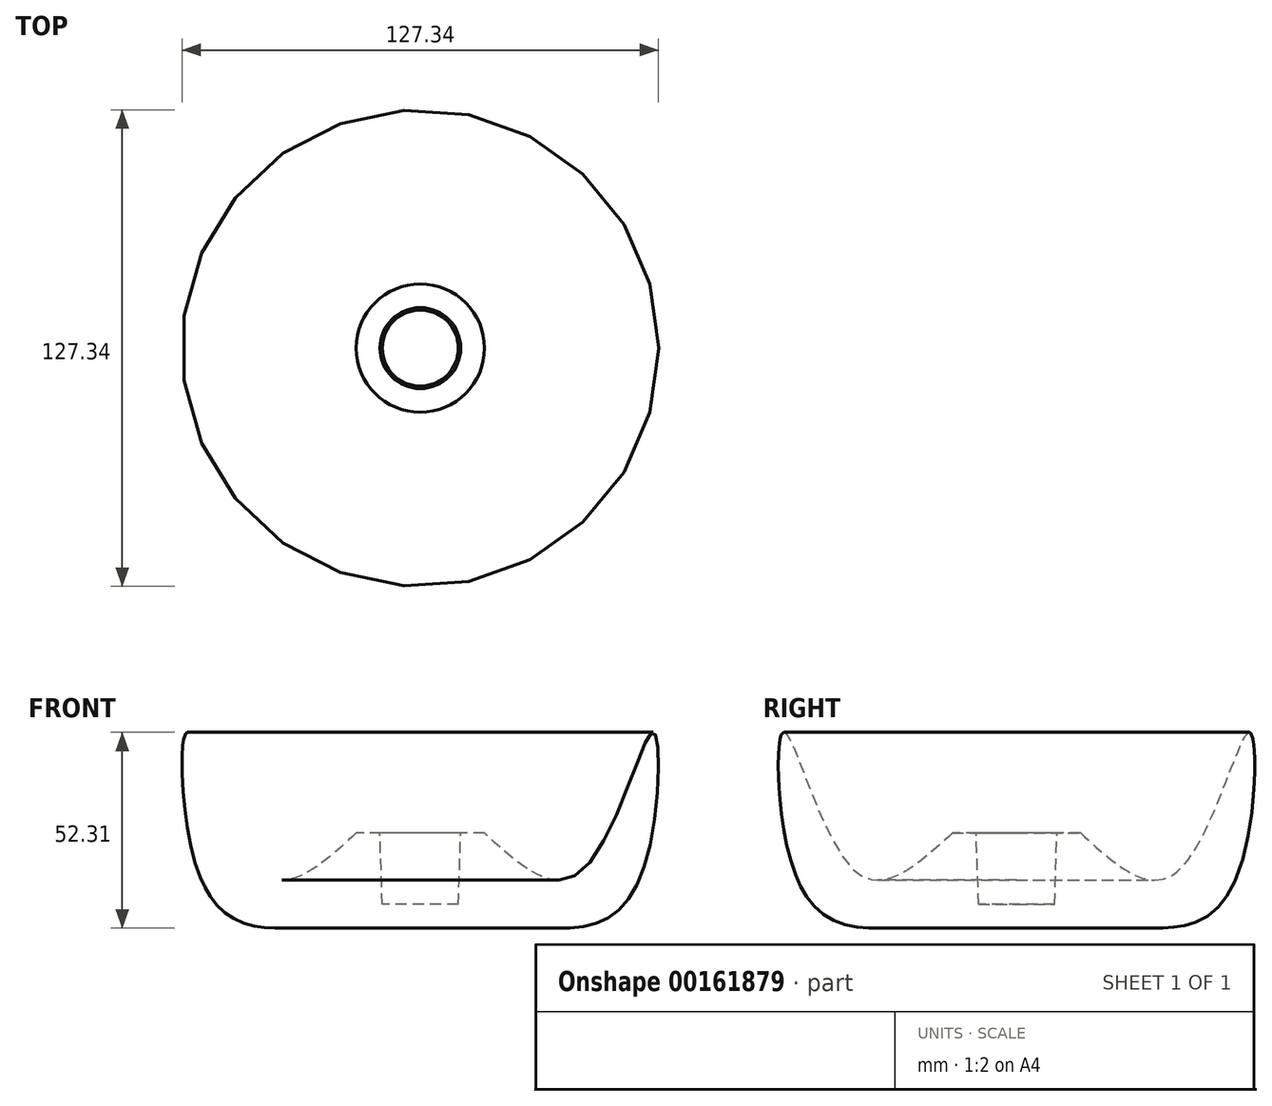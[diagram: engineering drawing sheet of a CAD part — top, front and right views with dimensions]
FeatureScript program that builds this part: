
annotation { "Feature Type Name" : "Feature", "Feature Type Description" : "" }
export const myFeature = defineFeature(function(context is Context, id is Id, definition is map)
    precondition{}
    {
        {
            var Q0;
            Q0=qCreatedBy(makeId("Front.planeOp"),FACE);
            var sketch = newSketch(context, id + "F0", { "sketchPlane" : qUnion([Q0])});
            skLineSegment(sketch, "E0", {"start": v(0, 0) * mm, "end": v(10.16, 0) * mm});
            skLineSegment(sketch, "E1", {"start": v(10.16, 0) * mm, "end": v(10.8, 19.05) * mm});
            skLineSegment(sketch, "E2", {"start": v(10.8, 19.05) * mm, "end": v(0, 19.05) * mm});
            skLineSegment(sketch, "E3", {"start": v(0, 19.05) * mm, "end": v(0, 0) * mm});
            skLineSegment(sketch, "E4", {"start": v(10.8, 19.05) * mm, "end": v(17.14, 19.05) * mm});
            skLineSegment(sketch, "E5", {"start": v(17.14, 19.05) * mm, "end": v(17.14, 0) * mm});
            skLineSegment(sketch, "E6", {"start": v(17.14, 0) * mm, "end": v(17.14, -6.35) * mm});
            skLineSegment(sketch, "E7", {"start": v(17.14, -6.35) * mm, "end": v(0, -6.35) * mm});
            skLineSegment(sketch, "E8", {"start": v(0, -6.35) * mm, "end": v(0, 0) * mm});
            skLineSegment(sketch, "E9", {"start": v(17.14, -6.35) * mm, "end": v(36.2, -6.35) * mm});
            skFitSpline(sketch, "E10", {"points": [v(36.2, -6.35) * mm, v(50.05, -3.68) * mm, v(61.49, 16.23) * mm, v(62, 45.92) * mm, v(42.59, 8.47) * mm, v(17.14, 19.05) * mm], "startDerivative": vector(103.43, 0) * mm, "endDerivative": vector(-131.77, 121.1) * mm});
            skSolve(sketch);
        }
        {
            var Q0;
            Q0=makeQuery(id+"F0.imprint","IMPRINT",FACE,{"disambiguationData":[TD([[makeQuery(id+"F0.imprint","IMPRINT",EDGE,{"derivedFrom":sQuery(id+"F0.wireOp",EDGE,"E0")}),-1.0]])]});
            var Q1;
            Q1=makeQuery(id+"F0.imprint","IMPRINT",FACE,{"disambiguationData":[TD([[makeQuery(id+"F0.imprint","IMPRINT",EDGE,{"derivedFrom":sQuery(id+"F0.wireOp",EDGE,"E5")}),1.0]])]});
            var Q2;
            Q2=sQuery(id+"F0.wireOp",EDGE,"E3");
            revolve(context, id + "F1", {"entities" : qUnion([Q0, Q1]), "axis" : qUnion([Q2]), "revolveType" : RevolveType.FULL});
        }
        {
            var Q0;
            Q0=makeQuery(id+"F1.opRevolve","SWEPT_FACE",FACE,{"disambiguationData":[OSD([sQuery(id+"F0.wireOp",EDGE,"E7"),sQuery(id+"F0.wireOp",EDGE,"E9")])]});
            var sketch = newSketch(context, id + "F2", { "sketchPlane" : qUnion([Q0])});
            skLineSegment(sketch, "E11.bottom", {"start": v(-93.1, -77.7) * mm, "end": v(94.17, -77.7) * mm});
            skLineSegment(sketch, "E11.top", {"start": v(-93.1, 73.67) * mm, "end": v(94.17, 73.67) * mm});
            skLineSegment(sketch, "E11.left", {"start": v(-93.1, -77.7) * mm, "end": v(-93.1, 73.67) * mm});
            skLineSegment(sketch, "E11.right", {"start": v(94.17, -77.7) * mm, "end": v(94.17, 73.67) * mm});
            skSolve(sketch);
        }
        {
            var Q0;
            Q0=makeQuery(id+"F2.imprint","IMPRINT",FACE,{"disambiguationData":[TD([[makeQuery(id+"F2.imprint","IMPRINT",EDGE,{"derivedFrom":sQuery(id+"F2.wireOp",EDGE,"E11.bottom")}),1.0]])]});
            var Q1;
            Q1=makeQuery(id+"F2.imprint","IMPRINT",FACE,{"disambiguationData":[TD([[makeQuery(id+"F2.imprint","IMPRINT",EDGE,{"derivedFrom":makeQuery(id+"F1.opRevolve","SWEPT_EDGE",EDGE,{"disambiguationData":[OSD([sQuery(id+"F0.wireOp",EDGE,"E9"),sQuery(id+"F0.wireOp",EDGE,"E10")])]})}),-1.0]])]});
            extrude(context, id + "F3", {"entities" : qUnion([Q0, Q1]), "operationType" : NewBodyOperationType.REMOVE, "depth" : 25.4 * mm});
        }
    });
